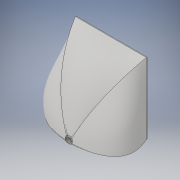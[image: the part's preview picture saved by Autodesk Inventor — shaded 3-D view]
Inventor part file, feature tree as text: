
AUTODESK INVENTOR PART (.ipt)
format: ipt  version: 2017 (Build 210142000, 142)  size: 411,136 bytes
history: native  units: in
note: dims shown in document units (in); Inventor stores cm internally (conversion verified against a paired STEP export)
features: sketch x4, extrude x2, other x2, loft x2
ambient origin geometry x8: Origin, YZ Plane, XZ Plane, XY Plane, X Axis, Y Axis, Z Axis, Center Point
bodies: Solid1 (feature_tree)
feature tree (10):
  extrude  "connection"  Depth=1.0in
  other  "front half of room"
  sketch  "Sketch2"  dims[d17=30.0in d26=69.0in d27=59.0in d28=102.0in]
  other  "front of room"
  sketch  "Sketch3"  dims[d29=102.0in d33=1.0in d34=1.0in]
  loft  "shell make "
  loft  "shell cut"
  extrude  "connection to door"  Depth=1.0in
  sketch  "Sketch1"  dims[d12=1.0in d13=0.0in d14=30.0in]
  sketch  "Sketch5"  dims[d35=1.0in d36=1.0in d55=100.0in d56=100.0in d57=1.0in d58=0.0in d82=4.0in d83=1.0in d84=4.8944in d85=0.5833in d86=3.8873in d87=3.8873in d88=1.7083in d89=0.0625in d90=0.0625in d91=1.6458in d92=0.125in d93=0.125in d151=70.0in d152=60.0in d153=69.0in d154=59.0in d157=0.0in d158=90.0deg d159=0.0in d160=90.0deg d161=0.0in d162=90.0deg d179=1.0in d180=0.0in d181=90.0deg d182=0.0in d183=90.0deg d184=0.0in d185=90.0deg d217=54.4672in]
